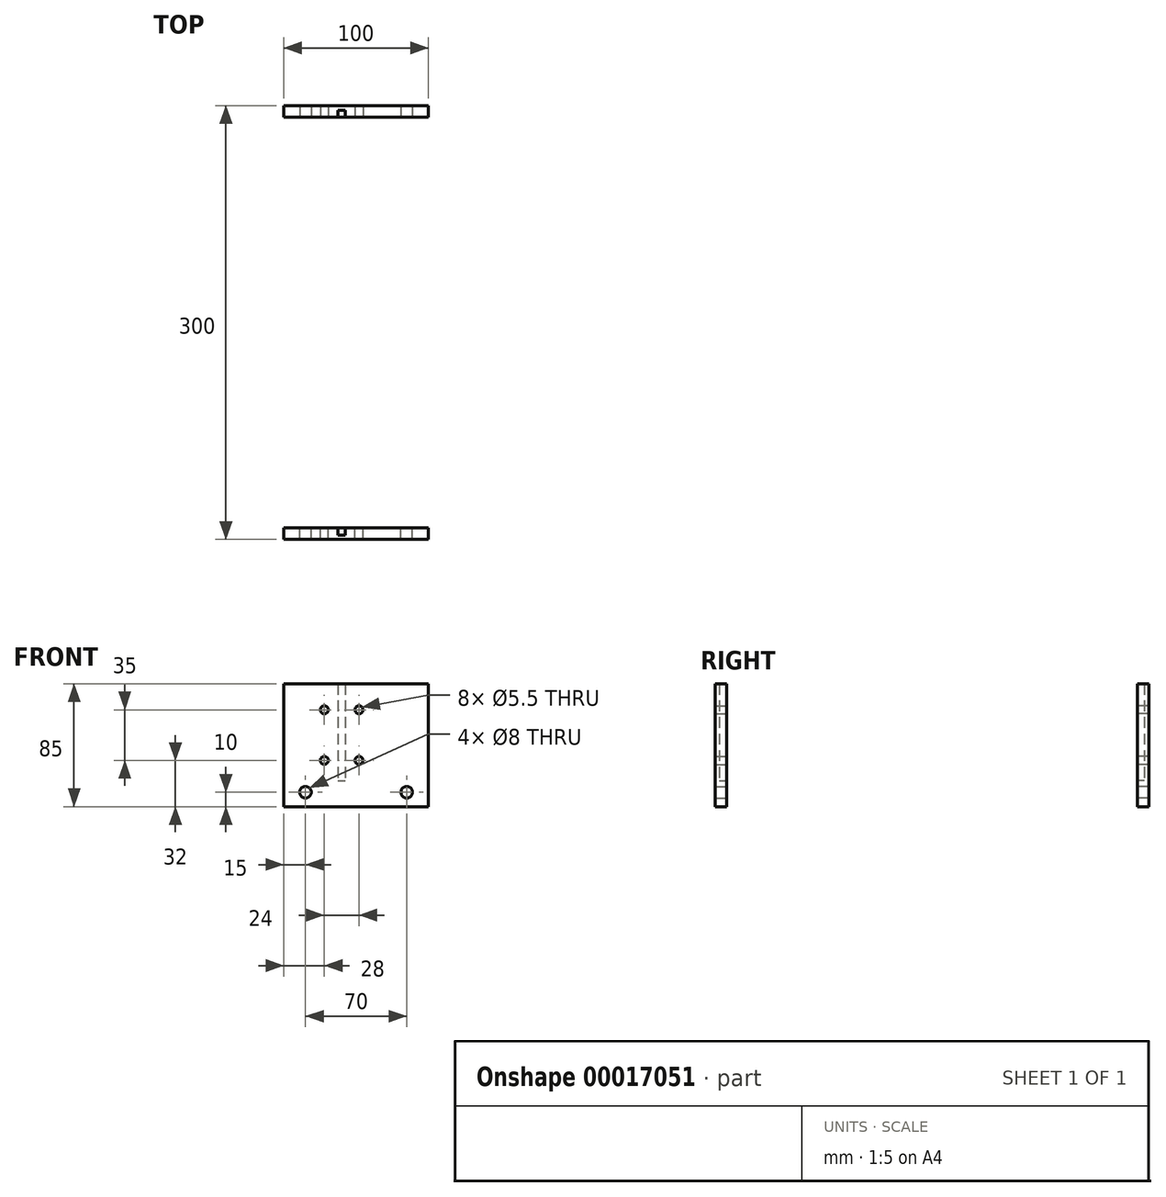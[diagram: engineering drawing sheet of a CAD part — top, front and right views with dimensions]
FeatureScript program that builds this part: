
annotation { "Feature Type Name" : "Feature", "Feature Type Description" : "" }
export const myFeature = defineFeature(function(context is Context, id is Id, definition is map)
    precondition{}
    {
        {
            var Q0;
            Q0=qCreatedBy(makeId("Front.planeOp"),FACE);
            var sketch = newSketch(context, id + "F0", { "sketchPlane" : qUnion([Q0])});
            skLineSegment(sketch, "E0.bottom", {"start": v(50, 50) * mm, "end": v(-50, 50) * mm});
            skLineSegment(sketch, "E0.top", {"start": v(50, -60) * mm, "end": v(-50, -60) * mm});
            skLineSegment(sketch, "E0.left", {"start": v(50, 50) * mm, "end": v(50, -60) * mm});
            skLineSegment(sketch, "E0.right", {"start": v(-50, 50) * mm, "end": v(-50, -60) * mm});
            skSolve(sketch);
        }
        {
            var Q0;
            Q0 = qSketchRegion(id + "F0", true);
            extrude(context, id + "F1", {"entities" : qUnion([Q0]), "depth" : 8 * mm});
        }
        {
            var Q0;
            Q0=makeQuery(id+"F1.opExtrude","CAP_FACE",FACE,{"disambiguationData":[OSD([sQuery(id+"F0.wireOp",EDGE,"E0.bottom"),sQuery(id+"F0.wireOp",EDGE,"E0.top"),sQuery(id+"F0.wireOp",EDGE,"E0.left"),sQuery(id+"F0.wireOp",EDGE,"E0.right")])],"isStart":false});
            var sketch = newSketch(context, id + "F2", { "sketchPlane" : qUnion([Q0])});
            skLineSegment(sketch, "E1.left", {"start": v(-12.5, 50.45) * mm, "end": v(-12.5, -42) * mm});
            skLineSegment(sketch, "E1.right", {"start": v(-7.45, 50.45) * mm, "end": v(-7.45, -42) * mm});
            skLineSegment(sketch, "E2", {"start": v(-12.5, 50.45) * mm, "end": v(-7.45, 50.45) * mm});
            skLineSegment(sketch, "E3", {"start": v(-12.5, -42) * mm, "end": v(-7.45, -42) * mm});
            skPoint(sketch, "E1.top.start.orphan", {"position": v(-12.5, -60) * mm});
            skSolve(sketch);
        }
        {
            var Q0;
            Q0 = qSketchRegion(id + "F2", true);
            extrude(context, id + "F3", {"entities" : qUnion([Q0]), "operationType" : NewBodyOperationType.REMOVE, "oppositeDirection" : true, "depth" : 5 * mm});
        }
        {
            var Q0;
            {var subQ0=sQuery(id+"F0.wireOp",EDGE,"E0.bottom");var subQ1=sQuery(id+"F0.wireOp",EDGE,"E0.top");var subQ2=sQuery(id+"F0.wireOp",EDGE,"E0.right");Q0=makeQuery(id+"F3.boolean.opBoolean","SPLIT",FACE,{"disambiguationData":[TD([makeQuery(id+"F1.opExtrude","SWEPT_FACE",FACE,{"disambiguationData":[OSD([subQ2])]})])],"derivedFrom":makeQuery(id+"F1.opExtrude","CAP_FACE",FACE,{"disambiguationData":[OSD([subQ0,subQ1,sQuery(id+"F0.wireOp",EDGE,"E0.left"),subQ2])],"isStart":false})});}
            var sketch = newSketch(context, id + "F4", { "sketchPlane" : qUnion([Q0])});
            skCircle(sketch, "E4", {"center": v(-35, -50) * mm, "radius": 4 * mm});
            skCircle(sketch, "E5", {"center": v(35, -50) * mm, "radius": 4 * mm});
            skSolve(sketch);
        }
        {
            var Q0;
            Q0 = qSketchRegion(id + "F4", true);
            extrude(context, id + "F5", {"entities" : qUnion([Q0]), "operationType" : NewBodyOperationType.REMOVE, "endBound" : BoundingType.THROUGH_ALL, "oppositeDirection" : true, "depth" : 25 * mm});
        }
        {
            var Q0;
            {var subQ0=sQuery(id+"F0.wireOp",EDGE,"E0.bottom");var subQ1=sQuery(id+"F0.wireOp",EDGE,"E0.top");var subQ2=sQuery(id+"F0.wireOp",EDGE,"E0.right");Q0=makeQuery(id+"F3.boolean.opBoolean","SPLIT",FACE,{"disambiguationData":[TD([makeQuery(id+"F1.opExtrude","SWEPT_FACE",FACE,{"disambiguationData":[OSD([subQ2])]})])],"derivedFrom":makeQuery(id+"F1.opExtrude","CAP_FACE",FACE,{"disambiguationData":[OSD([subQ0,subQ1,sQuery(id+"F0.wireOp",EDGE,"E0.left"),subQ2])],"isStart":false})});}
            var sketch = newSketch(context, id + "F6", { "sketchPlane" : qUnion([Q0])});
            skCircle(sketch, "E6", {"center": v(-22, -28) * mm, "radius": 2.75 * mm});
            skCircle(sketch, "E7", {"center": v(-22, 7) * mm, "radius": 2.75 * mm});
            skCircle(sketch, "E8", {"center": v(2, 7) * mm, "radius": 2.75 * mm});
            skCircle(sketch, "E9", {"center": v(2, -28) * mm, "radius": 2.75 * mm});
            skSolve(sketch);
        }
        {
            var Q0;
            Q0 = qSketchRegion(id + "F6", true);
            extrude(context, id + "F7", {"entities" : qUnion([Q0]), "operationType" : NewBodyOperationType.REMOVE, "endBound" : BoundingType.THROUGH_ALL, "oppositeDirection" : true, "depth" : 25 * mm});
        }
        {
            var Q0;
            Q0=qCreatedBy(makeId("Front.planeOp"),FACE);
            cPlane(context, id + "F8", {"entities" : qUnion([Q0]), "cplaneType" : CPlaneType.OFFSET, "offset" : 150 * mm, "width" : 150 * mm, "height" : 150 * mm});
        }
        {
            var Q0;
            Q0=makeQuery(id+"F1.opExtrude","CAP_FACE",FACE,{"disambiguationData":[OSD([sQuery(id+"F0.wireOp",EDGE,"E0.bottom"),sQuery(id+"F0.wireOp",EDGE,"E0.top"),sQuery(id+"F0.wireOp",EDGE,"E0.left"),sQuery(id+"F0.wireOp",EDGE,"E0.right")])],"isStart":true});
            var sketch = newSketch(context, id + "F9", { "sketchPlane" : qUnion([Q0])});
            skLineSegment(sketch, "E10.bottom", {"start": v(-50, 50) * mm, "end": v(50, 50) * mm});
            skLineSegment(sketch, "E10.top", {"start": v(-50, 25) * mm, "end": v(50, 25) * mm});
            skLineSegment(sketch, "E10.left", {"start": v(-50, 50) * mm, "end": v(-50, 25) * mm});
            skLineSegment(sketch, "E10.right", {"start": v(50, 50) * mm, "end": v(50, 25) * mm});
            skSolve(sketch);
        }
        {
            var Q0;
            Q0 = qSketchRegion(id + "F9", true);
            extrude(context, id + "F10", {"entities" : qUnion([Q0]), "operationType" : NewBodyOperationType.REMOVE, "endBound" : BoundingType.THROUGH_ALL, "oppositeDirection" : true, "depth" : 25 * mm});
        }
        {
            var Q0;
            Q0=makeQuery(id+"F1.opExtrude","SWEPT_BODY",BODY,{"disambiguationData":[OSD([sQuery(id+"F0.wireOp",EDGE,"E0.bottom"),sQuery(id+"F0.wireOp",EDGE,"E0.top"),sQuery(id+"F0.wireOp",EDGE,"E0.left"),sQuery(id+"F0.wireOp",EDGE,"E0.right")])]});
            var Q1;
            Q1=qCreatedBy(id+"F8.planeOp",FACE);
            mirror(context, id + "F11", {"entities" : qUnion([Q0]), "mirrorPlane" : qUnion([Q1])});
        }
    });
